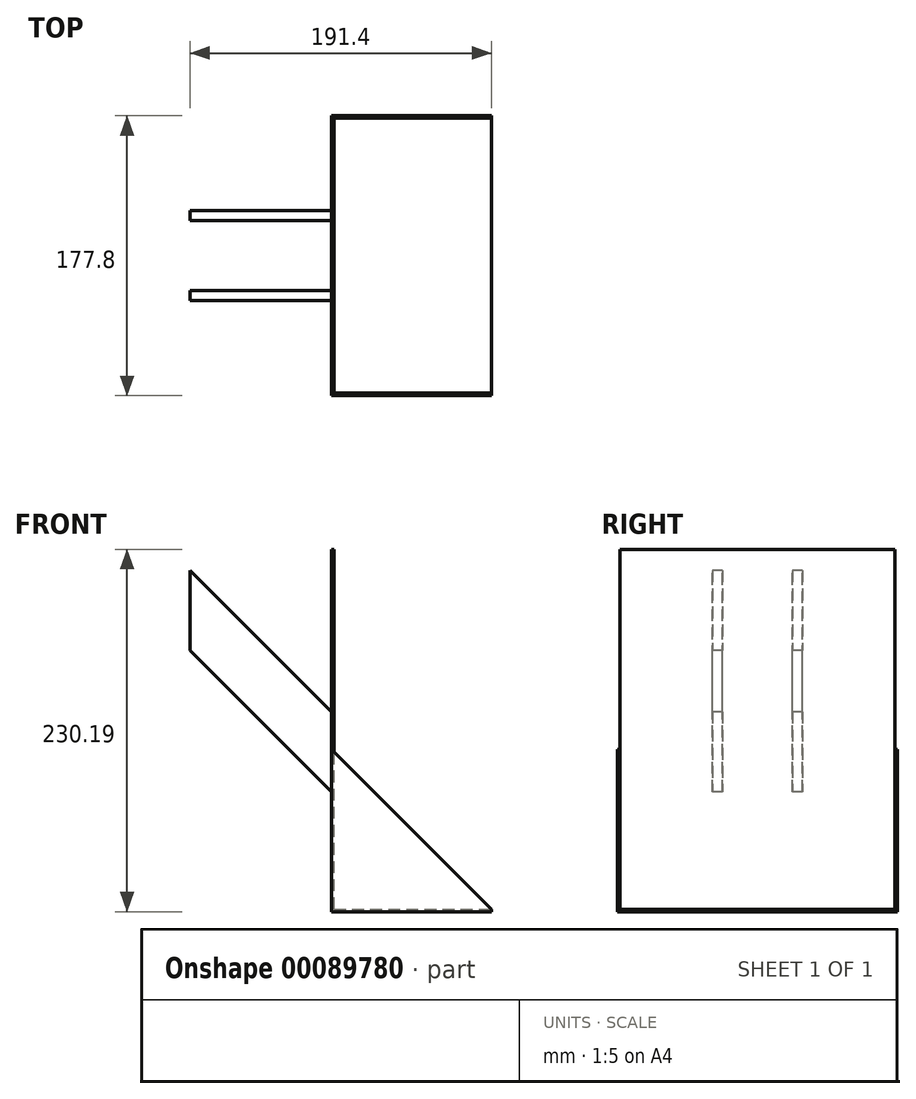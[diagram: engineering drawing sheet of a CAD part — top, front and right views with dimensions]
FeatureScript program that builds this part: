
annotation { "Feature Type Name" : "Feature", "Feature Type Description" : "" }
export const myFeature = defineFeature(function(context is Context, id is Id, definition is map)
    precondition{}
    {
        {
            var Q0;
            Q0=qCreatedBy(makeId("Top.planeOp"),FACE);
            var sketch = newSketch(context, id + "F0", { "sketchPlane" : qUnion([Q0])});
            skLineSegment(sketch, "E0.bottom", {"start": v(0, 0) * mm, "end": v(101.6, 0) * mm});
            skLineSegment(sketch, "E0.top", {"start": v(0, 177.8) * mm, "end": v(101.6, 177.8) * mm});
            skLineSegment(sketch, "E0.left", {"start": v(0, 0) * mm, "end": v(0, 177.8) * mm});
            skLineSegment(sketch, "E0.right", {"start": v(101.6, 0) * mm, "end": v(101.6, 177.8) * mm});
            skSolve(sketch);
        }
        {
            var Q0;
            Q0=makeQuery(id+"F0.imprint","IMPRINT",FACE,{"disambiguationData":[TD([[makeQuery(id+"F0.imprint","IMPRINT",EDGE,{"derivedFrom":sQuery(id+"F0.wireOp",EDGE,"E0.bottom")}),1.0]])]});
            extrude(context, id + "F1", {"entities" : qUnion([Q0]), "depth" : 1.59 * mm});
        }
        {
            var Q0;
            Q0=qCreatedBy(makeId("Front.planeOp"),FACE);
            var sketch = newSketch(context, id + "F2", { "sketchPlane" : qUnion([Q0])});
            skLineSegment(sketch, "E1", {"start": v(0, 1.59) * mm, "end": v(0, 103.19) * mm});
            skLineSegment(sketch, "E2", {"start": v(0, 1.59) * mm, "end": v(101.6, 1.59) * mm});
            skLineSegment(sketch, "E3", {"start": v(0, 103.19) * mm, "end": v(101.6, 1.59) * mm});
            skSolve(sketch);
        }
        {
            var Q0;
            Q0=makeQuery(id+"F2.imprint","IMPRINT",FACE,{"disambiguationData":[TD([[makeQuery(id+"F2.imprint","IMPRINT",EDGE,{"derivedFrom":sQuery(id+"F2.wireOp",EDGE,"E1")}),-1.0]])]});
            extrude(context, id + "F3", {"entities" : qUnion([Q0]), "operationType" : NewBodyOperationType.ADD, "oppositeDirection" : true, "depth" : 1.59 * mm});
        }
        {
            var Q0;
            Q0=makeQuery(id+"F1.opExtrude","SWEPT_FACE",FACE,{"disambiguationData":[OSD([sQuery(id+"F0.wireOp",EDGE,"E0.top")])]});
            var sketch = newSketch(context, id + "F4", { "sketchPlane" : qUnion([Q0])});
            skLineSegment(sketch, "E4", {"start": v(0, 1.59) * mm, "end": v(0, 103.19) * mm});
            skLineSegment(sketch, "E5", {"start": v(0, 1.59) * mm, "end": v(-101.6, 1.59) * mm});
            skLineSegment(sketch, "E6", {"start": v(0, 103.19) * mm, "end": v(-101.6, 1.59) * mm});
            skSolve(sketch);
        }
        {
            var Q0;
            Q0=makeQuery(id+"F4.imprint","IMPRINT",FACE,{"disambiguationData":[TD([[makeQuery(id+"F4.imprint","IMPRINT",EDGE,{"derivedFrom":sQuery(id+"F4.wireOp",EDGE,"E4")}),1.0]])]});
            extrude(context, id + "F5", {"entities" : qUnion([Q0]), "operationType" : NewBodyOperationType.ADD, "oppositeDirection" : true, "depth" : 1.59 * mm});
        }
        {
            var Q0;
            Q0=makeQuery(id+"F5.boolean.opBoolean","MERGE",FACE,{"derivedFrom":[makeQuery(id+"F3.boolean.opBoolean","MERGE",FACE,{"derivedFrom":[makeQuery(id+"F1.opExtrude","SWEPT_FACE",FACE,{"disambiguationData":[OSD([sQuery(id+"F0.wireOp",EDGE,"E0.left")])]}),makeQuery(id+"F3.opExtrude","SWEPT_FACE",FACE,{"disambiguationData":[OSD([sQuery(id+"F2.wireOp",EDGE,"E1")])]})]}),makeQuery(id+"F5.opExtrude","SWEPT_FACE",FACE,{"disambiguationData":[OSD([sQuery(id+"F4.wireOp",EDGE,"E4")])]})]});
            var sketch = newSketch(context, id + "F6", { "sketchPlane" : qUnion([Q0])});
            skLineSegment(sketch, "E7.bottom", {"start": v(-1.59, 1.59) * mm, "end": v(-176.21, 1.59) * mm});
            skLineSegment(sketch, "E7.top", {"start": v(-1.59, 230.19) * mm, "end": v(-176.21, 230.19) * mm});
            skLineSegment(sketch, "E7.left", {"start": v(-1.59, 1.59) * mm, "end": v(-1.59, 230.19) * mm});
            skLineSegment(sketch, "E7.right", {"start": v(-176.21, 1.59) * mm, "end": v(-176.21, 230.19) * mm});
            skSolve(sketch);
        }
        {
            var Q0;
            {var subQ5=sQuery(id+"F6.wireOp",EDGE,"E7.bottom");Q0=makeQuery(id+"F6.imprint","IMPRINT",FACE,{"disambiguationData":[TD([[makeQuery(id+"F6.imprint","IMPRINT",EDGE,{"derivedFrom":subQ5}),-1.0]])]});}
            extrude(context, id + "F7", {"entities" : qUnion([Q0]), "operationType" : NewBodyOperationType.ADD, "oppositeDirection" : true, "depth" : 1.59 * mm});
        }
        {
            var Q0;
            Q0=makeQuery(id+"F7.boolean.opBoolean","MERGE",FACE,{"derivedFrom":[makeQuery(id+"F5.boolean.opBoolean","MERGE",FACE,{"derivedFrom":[makeQuery(id+"F3.boolean.opBoolean","MERGE",FACE,{"derivedFrom":[makeQuery(id+"F1.opExtrude","SWEPT_FACE",FACE,{"disambiguationData":[OSD([sQuery(id+"F0.wireOp",EDGE,"E0.left")])]}),makeQuery(id+"F3.opExtrude","SWEPT_FACE",FACE,{"disambiguationData":[OSD([sQuery(id+"F2.wireOp",EDGE,"E1")])]})]}),makeQuery(id+"F5.opExtrude","SWEPT_FACE",FACE,{"disambiguationData":[OSD([sQuery(id+"F4.wireOp",EDGE,"E4")])]})]}),makeQuery(id+"F7.opExtrude","CAP_FACE",FACE,{"disambiguationData":[OSD([sQuery(id+"F6.wireOp",EDGE,"E7.bottom"),sQuery(id+"F6.wireOp",EDGE,"E7.top"),sQuery(id+"F6.wireOp",EDGE,"E7.left"),sQuery(id+"F6.wireOp",EDGE,"E7.right")])],"isStart":true})]});
            var sketch = newSketch(context, id + "F8", { "sketchPlane" : qUnion([Q0])});
            skLineSegment(sketch, "E8.bottom", {"start": v(-117.48, 127) * mm, "end": v(-111.13, 127) * mm});
            skLineSegment(sketch, "E8.top", {"start": v(-117.48, 76.2) * mm, "end": v(-111.13, 76.2) * mm});
            skLineSegment(sketch, "E8.left", {"start": v(-117.48, 127) * mm, "end": v(-117.48, 76.2) * mm});
            skLineSegment(sketch, "E8.right", {"start": v(-111.13, 127) * mm, "end": v(-111.13, 76.2) * mm});
            skLineSegment(sketch, "E9.bottom", {"start": v(-66.68, 127) * mm, "end": v(-60.33, 127) * mm});
            skLineSegment(sketch, "E9.top", {"start": v(-66.68, 76.2) * mm, "end": v(-60.32, 76.2) * mm});
            skLineSegment(sketch, "E9.left", {"start": v(-66.68, 127) * mm, "end": v(-66.68, 76.2) * mm});
            skLineSegment(sketch, "E9.right", {"start": v(-60.33, 127) * mm, "end": v(-60.33, 76.2) * mm});
            skLineSegment(sketch, "E10", {"start": v(-88.9, 230.19) * mm, "end": v(-88.9, 203.7) * mm});
            skSolve(sketch);
        }
        {
            var Q0;
            Q0=makeQuery(id+"F5.boolean.opBoolean","MERGE",FACE,{"derivedFrom":[makeQuery(id+"F1.opExtrude","SWEPT_FACE",FACE,{"disambiguationData":[OSD([sQuery(id+"F0.wireOp",EDGE,"E0.top")])]}),makeQuery(id+"F5.opExtrude","CAP_FACE",FACE,{"disambiguationData":[OSD([sQuery(id+"F4.wireOp",EDGE,"E4"),sQuery(id+"F4.wireOp",EDGE,"E5"),sQuery(id+"F4.wireOp",EDGE,"E6")])],"isStart":true})]});
            cPlane(context, id + "F9", {"entities" : qUnion([Q0]), "cplaneType" : CPlaneType.OFFSET, "offset" : (3.5 + (1.75 / 2)) * mm, "oppositeDirection" : true, "width" : 152.4 * mm, "height" : 152.4 * mm});
        }
        {
            var Q0;
            Q0=qCreatedBy(id+"F9.planeOp",FACE);
            var sketch = newSketch(context, id + "F10", { "sketchPlane" : qUnion([Q0])});
            skLineSegment(sketch, "E11", {"start": v(0, 76.2) * mm, "end": v(89.8, 166) * mm});
            skSolve(sketch);
        }
        {
            var Q0;
            Q0=makeQuery(id+"F8.imprint","IMPRINT",FACE,{"disambiguationData":[TD([[makeQuery(id+"F8.imprint","IMPRINT",EDGE,{"derivedFrom":sQuery(id+"F8.wireOp",EDGE,"E9.bottom")}),-1.0]])]});
            var Q1;
            Q1=makeQuery(id+"F8.imprint","IMPRINT",FACE,{"disambiguationData":[TD([[makeQuery(id+"F8.imprint","IMPRINT",EDGE,{"derivedFrom":sQuery(id+"F8.wireOp",EDGE,"E8.bottom")}),-1.0]])]});
            var Q2;
            Q2=sQuery(id+"F10.wireOp",EDGE,"E11");
            sweep(context, id + "F11", {"operationType" : NewBodyOperationType.ADD, "profiles" : qUnion([Q0, Q1]), "path" : qUnion([Q2])});
        }
    });
